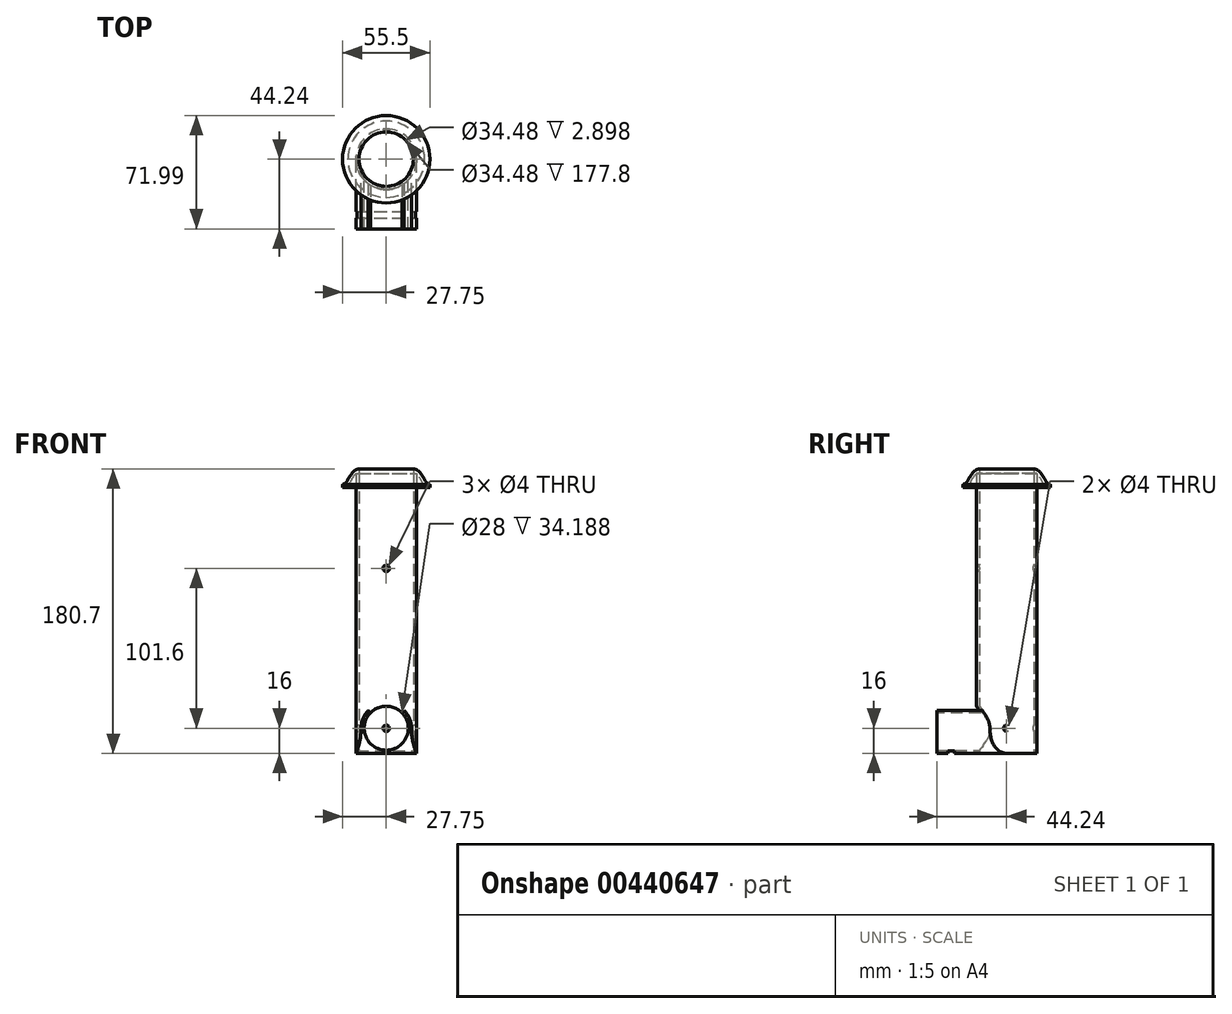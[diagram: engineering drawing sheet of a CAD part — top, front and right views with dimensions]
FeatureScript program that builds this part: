
annotation { "Feature Type Name" : "Feature", "Feature Type Description" : "" }
export const myFeature = defineFeature(function(context is Context, id is Id, definition is map)
    precondition{}
    {
        {
            var Q0;
            Q0=qCreatedBy(makeId("Top.planeOp"),FACE);
            var sketch = newSketch(context, id + "F0", { "sketchPlane" : qUnion([Q0])});
            skCircle(sketch, "E0", {"center": v(0, 19.24) * mm, "radius": 17.24 * mm});
            skCircle(sketch, "E1", {"center": v(0, 19.24) * mm, "radius": 19.24 * mm});
            skSolve(sketch);
        }
        {
            var Q0;
            Q0=makeQuery(id+"F0.imprint","IMPRINT",FACE,{"disambiguationData":[TD([[makeQuery(id+"F0.imprint","IMPRINT",EDGE,{"derivedFrom":sQuery(id+"F0.wireOp",EDGE,"E0")}),-1.0]])]});
            extrude(context, id + "F1", {"entities" : qUnion([Q0]), "depth" : 177.8 * mm});
        }
        {
            var Q0;
            Q0=qCreatedBy(makeId("Front.planeOp"),FACE);
            var sketch = newSketch(context, id + "F2", { "sketchPlane" : qUnion([Q0])});
            skCircle(sketch, "E2", {"center": v(0, 16) * mm, "radius": 14 * mm});
            skArc(sketch, "E3", {"start": v(16, 16) * mm, "mid": v(0, 32) * mm, "end": v(-16, 16) * mm});
            skLineSegment(sketch, "E4", {"start": v(-19.24, 0) * mm, "end": v(-19.24, 35) * mm});
            skLineSegment(sketch, "E5", {"start": v(-19.24, 0) * mm, "end": v(19.24, 0) * mm});
            skArc(sketch, "E6", {"start": v(-19.24, 0) * mm, "mid": v(-16.82, 7.84) * mm, "end": v(-16, 16) * mm});
            skArc(sketch, "E7.MirrorCS", {"start": v(19.24, 0) * mm, "mid": v(16.82, 7.84) * mm, "end": v(16, 16) * mm});
            skSolve(sketch);
        }
        {
            var Q0;
            {var subQ0=sQuery(id+"F2.wireOp",EDGE,"E6");Q0=makeQuery(id+"F2.imprint","IMPRINT",FACE,{"disambiguationData":[TD([[makeQuery(id+"F2.imprint","IMPRINT",EDGE,{"derivedFrom":subQ0}),-1.0]])]});}
            var Q1;
            {var subQ6=sQuery(id+"F2.wireOp",EDGE,"E7.MirrorCS");Q1=makeQuery(id+"F2.imprint","IMPRINT",FACE,{"disambiguationData":[TD([[makeQuery(id+"F2.imprint","IMPRINT",EDGE,{"derivedFrom":subQ6}),1.0]])]});}
            var Q2;
            Q2=makeQuery(id+"F1.opExtrude","SWEPT_FACE",FACE,{"disambiguationData":[OSD([sQuery(id+"F0.wireOp",EDGE,"E1")])]});
            extrude(context, id + "F3", {"entities" : qUnion([Q0, Q1]), "operationType" : NewBodyOperationType.ADD, "depth" : 25 * mm, "hasSecondDirection" : true, "secondDirectionBound" : SecondDirectionBoundingType.UP_TO_SURFACE, "secondDirectionOppositeDirection" : true, "secondDirectionBoundEntityFace" : qUnion([Q2]), "secondDirectionDepth" : 12.3 * mm});
        }
        {
            var Q0;
            Q0=makeQuery(id+"F3.opExtrude","CAP_FACE",FACE,{"disambiguationData":[OSD([sQuery(id+"F2.wireOp",EDGE,"E2"),sQuery(id+"F2.wireOp",EDGE,"E3")])],"isStart":false});
            var sketch = newSketch(context, id + "F4", { "sketchPlane" : qUnion([Q0])});
            skCircle(sketch, "E8", {"center": v(0, 16) * mm, "radius": 14 * mm});
            skSolve(sketch);
        }
        {
            var Q0;
            Q0=makeQuery(id+"F4.imprint","IMPRINT",FACE,{"disambiguationData":[TD([[makeQuery(id+"F4.imprint","IMPRINT",EDGE,{"derivedFrom":sQuery(id+"F4.wireOp",EDGE,"E8")}),1.0]])]});
            var Q1;
            Q1=makeQuery(id+"F1.opExtrude","SWEPT_FACE",FACE,{"disambiguationData":[OSD([sQuery(id+"F0.wireOp",EDGE,"E0")])]});
            extrude(context, id + "F5", {"entities" : qUnion([Q0]), "operationType" : NewBodyOperationType.REMOVE, "endBound" : BoundingType.UP_TO_SURFACE, "oppositeDirection" : true, "endBoundEntityFace" : qUnion([Q1]), "depth" : 25 * mm});
        }
        {
            var Q0;
            Q0=makeQuery(id+"F3.opExtrude","CAP_FACE",FACE,{"disambiguationData":[OSD([sQuery(id+"F2.wireOp",EDGE,"E2"),sQuery(id+"F2.wireOp",EDGE,"E3")])],"isStart":false});
            var sketch = newSketch(context, id + "F6", { "sketchPlane" : qUnion([Q0])});
            skCircle(sketch, "E9", {"center": v(0, 16) * mm, "radius": 2 * mm});
            skCircle(sketch, "E10", {"center": v(0, 117.6) * mm, "radius": 2 * mm});
            skSolve(sketch);
        }
        {
            var Q0;
            Q0=makeQuery(id+"F6.imprint","IMPRINT",FACE,{"disambiguationData":[TD([[makeQuery(id+"F6.imprint","IMPRINT",EDGE,{"derivedFrom":sQuery(id+"F6.wireOp",EDGE,"E9")}),1.0]])]});
            var Q1;
            Q1=makeQuery(id+"F6.imprint","IMPRINT",FACE,{"disambiguationData":[TD([[makeQuery(id+"F6.imprint","IMPRINT",EDGE,{"derivedFrom":sQuery(id+"F6.wireOp",EDGE,"E10")}),1.0]])]});
            extrude(context, id + "F7", {"entities" : qUnion([Q0, Q1]), "operationType" : NewBodyOperationType.REMOVE, "endBound" : BoundingType.THROUGH_ALL, "oppositeDirection" : true, "depth" : 25 * mm});
        }
        {
            var Q0;
            Q0=makeQuery(id+"F3.opExtrude","CAP_FACE",FACE,{"disambiguationData":[OSD([sQuery(id+"F2.wireOp",EDGE,"E2"),sQuery(id+"F2.wireOp",EDGE,"E3")])],"isStart":false});
            var sketch = newSketch(context, id + "F8", { "sketchPlane" : qUnion([Q0])});
            skPoint(sketch, "E11.orphan", {"position": v(5.5, 40.82) * mm});
            skPoint(sketch, "E12.orphan", {"position": v(-5.5, 40.82) * mm});
            skLineSegment(sketch, "E13", {"start": v(-10, 25.8) * mm, "end": v(-11.41, 27.21) * mm});
            skArc(sketch, "E14", {"start": v(-11.41, 27.21) * mm, "mid": v(0, 32) * mm, "end": v(11.41, 27.21) * mm});
            skLineSegment(sketch, "E15.MirrorCS", {"start": v(10, 25.8) * mm, "end": v(11.41, 27.21) * mm});
            skPoint(sketch, "E16.orphan", {"position": v(-14.82, 30.62) * mm});
            skPoint(sketch, "E17.orphan", {"position": v(14.82, 30.62) * mm});
            skPoint(sketch, "E18.orphan", {"position": v(30.22, 5.1) * mm});
            skPoint(sketch, "E19.orphan", {"position": v(-30.22, 5.1) * mm});
            skArc(sketch, "E20", {"start": v(-10, 25.8) * mm, "mid": v(0, 30) * mm, "end": v(10, 25.8) * mm});
            skSolve(sketch);
        }
        {
            var Q0;
            Q0=makeQuery(id+"F8.imprint","IMPRINT",FACE,{"disambiguationData":[TD([[makeQuery(id+"F8.imprint","IMPRINT",EDGE,{"derivedFrom":sQuery(id+"F8.wireOp",EDGE,"E13")}),-1.0]])]});
            var Q1;
            {var subQ0=sQuery(id+"F0.wireOp",EDGE,"E1");Q1=makeQuery(id+"F3.boolean.opBoolean","SPLIT",FACE,{"disambiguationData":[TD([makeQuery(id+"F3.opExtrude","SWEPT_FACE",FACE,{"disambiguationData":[OSD([sQuery(id+"F2.wireOp",EDGE,"E3")])]})])],"derivedFrom":makeQuery(id+"F1.opExtrude","SWEPT_FACE",FACE,{"disambiguationData":[OSD([subQ0])]})});}
            extrude(context, id + "F9", {"entities" : qUnion([Q0]), "operationType" : NewBodyOperationType.REMOVE, "endBound" : BoundingType.UP_TO_SURFACE, "oppositeDirection" : true, "endBoundEntityFace" : qUnion([Q1]), "depth" : 25 * mm});
        }
        {
            var Q0;
            Q0=makeQuery(id+"F1.opExtrude","CAP_FACE",FACE,{"disambiguationData":[OSD([sQuery(id+"F0.wireOp",EDGE,"E0"),sQuery(id+"F0.wireOp",EDGE,"E1")])],"isStart":false});
            var sketch = newSketch(context, id + "F10", { "sketchPlane" : qUnion([Q0])});
            skCircle(sketch, "E21.0.0", {"center": v(0, 19.24) * mm, "radius": 19.24 * mm});
            skCircle(sketch, "E22.0", {"center": v(0, 19.24) * mm, "radius": 17.24 * mm});
            skSolve(sketch);
        }
        {
            var Q0;
            Q0=qCreatedBy(makeId("Right.planeOp"),FACE);
            var sketch = newSketch(context, id + "F11", { "sketchPlane" : qUnion([Q0])});
            skLineSegment(sketch, "E23", {"start": v(38.48, 177.8) * mm, "end": v(36.48, 177.8) * mm});
            skArc(sketch, "E24", {"start": v(0, 180.7) * mm, "mid": v(-3.78, 176.14) * mm, "end": v(-6.51, 170.88) * mm});
            skLineSegment(sketch, "E25", {"start": v(19.24, 160.88) * mm, "end": v(19.24, 222.73) * mm, "construction": true});
            skArc(sketch, "E26.0", {"start": v(0, 177.8) * mm, "mid": v(-3, 173.6) * mm, "end": v(-5.1, 168.88) * mm});
            skLineSegment(sketch, "E27", {"start": v(-6.51, 170.88) * mm, "end": v(-8.51, 170.88) * mm});
            skLineSegment(sketch, "E28", {"start": v(-8.5, 170.88) * mm, "end": v(-8.5, 168.88) * mm});
            skLineSegment(sketch, "E29", {"start": v(-8.51, 168.88) * mm, "end": v(-5.1, 168.88) * mm});
            skPoint(sketch, "E30.end.orphan", {"position": v(-6.38, 160.7) * mm});
            skPoint(sketch, "E30.start.orphan", {"position": v(-8.38, 160.7) * mm});
            skLineSegment(sketch, "E31", {"start": v(2, 177.8) * mm, "end": v(0, 177.8) * mm});
            skLineSegment(sketch, "E32", {"start": v(0, 180.7) * mm, "end": v(2, 180.7) * mm});
            skLineSegment(sketch, "E33", {"start": v(2, 180.7) * mm, "end": v(2, 177.8) * mm});
            skSolve(sketch);
        }
        {
            var Q0;
            {var subQ2=sQuery(id+"F11.wireOp",EDGE,"E24");Q0=makeQuery(id+"F11.imprint","IMPRINT",FACE,{"disambiguationData":[TD([[makeQuery(id+"F11.imprint","IMPRINT",EDGE,{"derivedFrom":subQ2}),1.0]])]});}
            var Q1;
            Q1=sQuery(id+"F11.wireOp",EDGE,"E25");
            revolve(context, id + "F12", {"entities" : qUnion([Q0]), "axis" : qUnion([Q1]), "revolveType" : RevolveType.FULL});
        }
        {
            var Q0;
            Q0=makeQuery(id+"F12.boolean.opBoolean","MERGE",EDGE,{"derivedFrom":[makeQuery(id+"FAofce050fpie5P_1.opExtrude","CAP_EDGE",EDGE,{"disambiguationData":[OSD([sQuery(id+"F10.wireOp",EDGE,"E21.0.0")])],"isStart":false}),makeQuery(id+"F12.opRevolve","SWEPT_EDGE",EDGE,{"disambiguationData":[OSD([sQuery(id+"F11.wireOp",EDGE,"843f5528-be57-4fd7-90cc-3219674f308401"),sQuery(id+"F11.wireOp",EDGE,"E24")])]})]});
            fillet(context, id + "F13", {"entities" : qUnion([Q0]), "radius" : 5 * mm, "tangentPropagation" : true, "allowEdgeOverflow" : false});
        }
        {
            var Q0;
            Q0=qCreatedBy(makeId("Right.planeOp"),FACE);
            cPlane(context, id + "F14", {"entities" : qUnion([Q0]), "cplaneType" : CPlaneType.OFFSET, "offset" : 46 * mm, "width" : 150 * mm, "height" : 150 * mm});
        }
        {
            var Q0;
            Q0=qCreatedBy(id+"F14.planeOp",FACE);
            var sketch = newSketch(context, id + "F15", { "sketchPlane" : qUnion([Q0])});
            skArc(sketch, "E34", {"start": v(7.09, 136.07) * mm, "mid": v(19.24, 133.25) * mm, "end": v(31.4, 136.07) * mm});
            skCircle(sketch, "E35", {"center": v(19.24, 168.73) * mm, "radius": 2 * mm});
            skSolve(sketch);
        }
        {
            var Q0;
            Q0=qCreatedBy(makeId("Right.planeOp"),FACE);
            var sketch = newSketch(context, id + "F16", { "sketchPlane" : qUnion([Q0])});
            skLineSegment(sketch, "E36", {"start": v(36.48, 14) * mm, "end": v(38.48, 14) * mm});
            skLineSegment(sketch, "E37", {"start": v(38.48, 18) * mm, "end": v(36.48, 18) * mm});
            skLineSegment(sketch, "E38", {"start": v(0, 119.6) * mm, "end": v(0, 177.8) * mm});
            skLineSegment(sketch, "E39", {"start": v(38.48, 177.8) * mm, "end": v(38.48, 119.6) * mm});
            skLineSegment(sketch, "E40", {"start": v(38.48, 115.6) * mm, "end": v(38.48, 18) * mm});
            skLineSegment(sketch, "E41", {"start": v(38.48, 14) * mm, "end": v(38.48, 0) * mm});
            skLineSegment(sketch, "E42", {"start": v(0, 30) * mm, "end": v(0, 115.6) * mm});
            skCircle(sketch, "E43", {"center": v(19.24, 16) * mm, "radius": 2 * mm});
            skLineSegment(sketch, "E44", {"start": v(0, 30) * mm, "end": v(0, 177.8) * mm});
            skLineSegment(sketch, "E45", {"start": v(38.48, 177.8) * mm, "end": v(38.48, 0) * mm});
            skLineSegment(sketch, "E46", {"start": v(0, 0) * mm, "end": v(38.48, 0) * mm, "construction": true});
            skPoint(sketch, "E47", {"position": v(19.24, 0) * mm});
            skLineSegment(sketch, "E48", {"start": v(38.48, 18) * mm, "end": v(38.48, 14) * mm, "construction": true});
            skPoint(sketch, "E49", {"position": v(38.48, 16) * mm});
            skLineSegment(sketch, "E50.bottom", {"start": v(-18, 0) * mm, "end": v(-14, 0) * mm});
            skLineSegment(sketch, "E50.top", {"start": v(-18, 1.5) * mm, "end": v(-14, 1.5) * mm});
            skLineSegment(sketch, "E50.left", {"start": v(-18, 0) * mm, "end": v(-18, 1.5) * mm});
            skLineSegment(sketch, "E50.right", {"start": v(-14, 0) * mm, "end": v(-14, 1.5) * mm});
            skSolve(sketch);
        }
        {
            var Q0;
            Q0=makeQuery(id+"F16.imprint","IMPRINT",FACE,{"disambiguationData":[TD([[makeQuery(id+"F16.imprint","IMPRINT",EDGE,{"derivedFrom":sQuery(id+"F16.wireOp",EDGE,"E43")}),1.0]])]});
            var Q1;
            Q1=makeQuery(id+"F16.imprint","IMPRINT",FACE,{"disambiguationData":[TD([[makeQuery(id+"F16.imprint","IMPRINT",EDGE,{"derivedFrom":sQuery(id+"F16.wireOp",EDGE,"E50.bottom")}),1.0]])]});
            extrude(context, id + "F17", {"entities" : qUnion([Q0, Q1]), "operationType" : NewBodyOperationType.REMOVE, "endBound" : BoundingType.SYMMETRIC, "oppositeDirection" : true, "depth" : 100 * mm});
        }
    });
